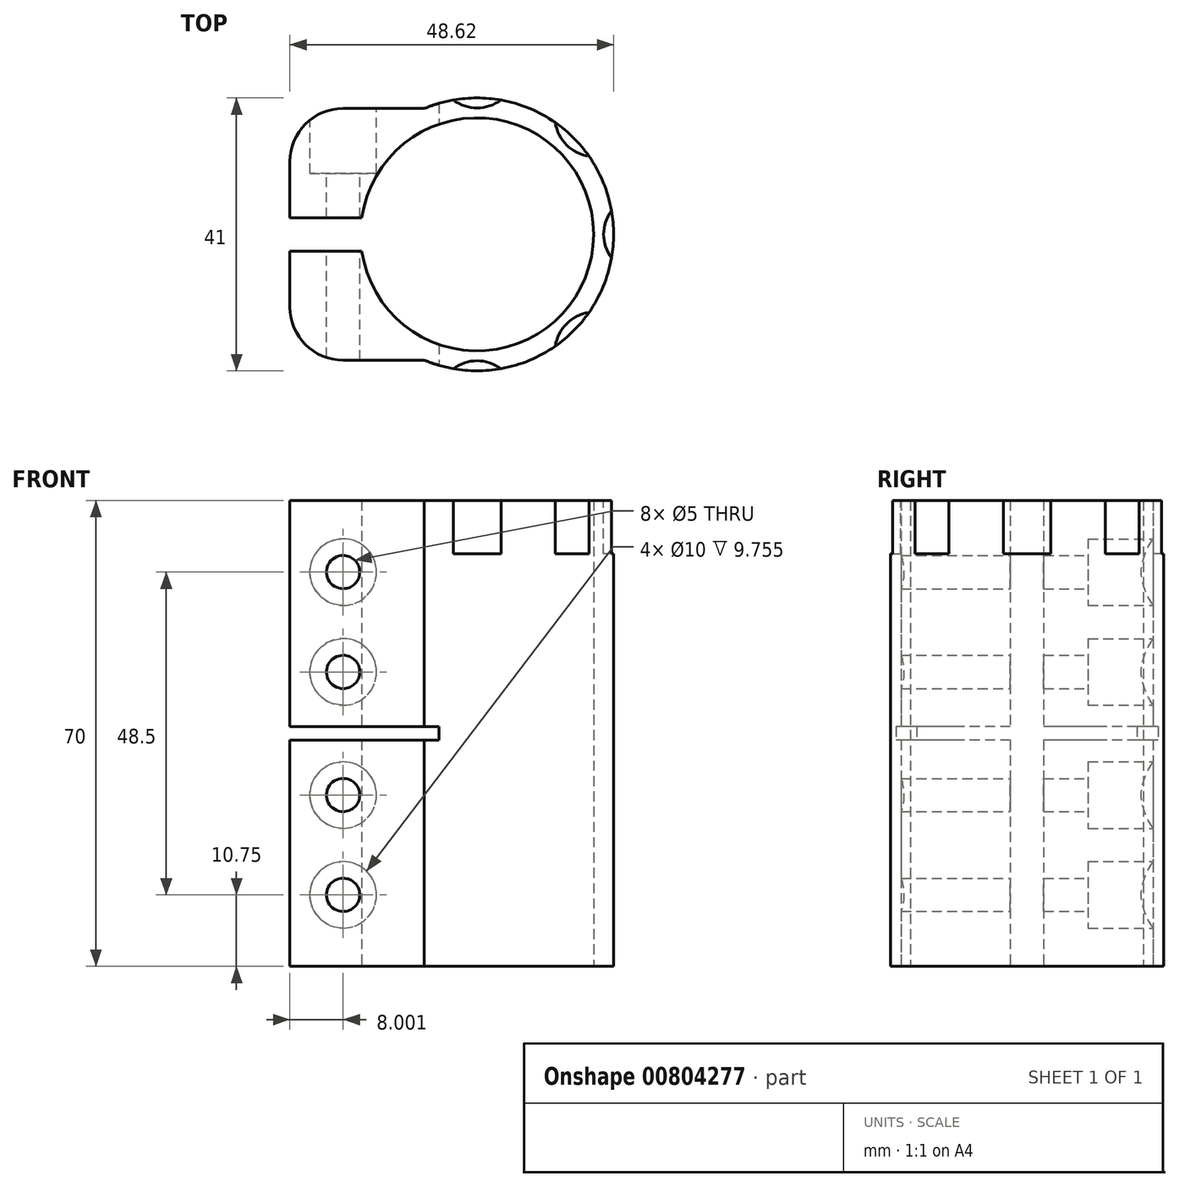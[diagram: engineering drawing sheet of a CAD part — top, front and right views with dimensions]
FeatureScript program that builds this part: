
annotation { "Feature Type Name" : "Feature", "Feature Type Description" : "" }
export const myFeature = defineFeature(function(context is Context, id is Id, definition is map)
    precondition{}
    {
        {
            var Q0;
            Q0=qCreatedBy(makeId("Top.planeOp"),FACE);
            var sketch = newSketch(context, id + "F0", { "sketchPlane" : qUnion([Q0])});
            skArc(sketch, "E0", {"start": v(-17.32, -2.5) * mm, "mid": v(17.5, 0) * mm, "end": v(-17.32, 2.5) * mm});
            skArc(sketch, "E1", {"start": v(-7.92, -18.9) * mm, "mid": v(20.5, 0) * mm, "end": v(-7.92, 18.9) * mm});
            skLineSegment(sketch, "E2", {"start": v(-17.32, 2.5) * mm, "end": v(-28.12, 2.5) * mm});
            skLineSegment(sketch, "E3", {"start": v(-28.12, 2.5) * mm, "end": v(-28.12, 10.9) * mm});
            skLineSegment(sketch, "E4", {"start": v(-20.12, 18.9) * mm, "end": v(-7.92, 18.9) * mm});
            skPoint(sketch, "E5.visualSharp", {"position": v(-28.12, 18.9) * mm});
            skArc(sketch, "E5.filletArc", {"start": v(-20.12, 18.9) * mm, "mid": v(-25.78, 16.57) * mm, "end": v(-28.12, 10.9) * mm});
            skLineSegment(sketch, "E6", {"start": v(0, 0) * mm, "end": v(42.18, 0) * mm, "construction": true});
            skLineSegment(sketch, "E7.MirrorCS", {"start": v(-20.12, -18.9) * mm, "end": v(-7.92, -18.9) * mm});
            skArc(sketch, "E8.MirrorCS", {"start": v(-20.12, -18.9) * mm, "mid": v(-25.78, -16.57) * mm, "end": v(-28.12, -10.9) * mm});
            skLineSegment(sketch, "E9.MirrorCS", {"start": v(-28.12, -2.5) * mm, "end": v(-28.12, -10.9) * mm});
            skLineSegment(sketch, "E10.MirrorCS", {"start": v(-17.32, -2.5) * mm, "end": v(-28.12, -2.5) * mm});
            skSolve(sketch);
        }
        {
            var Q0;
            Q0 = qSketchRegion(id + "F0", true);
            extrude(context, id + "F1", {"entities" : qUnion([Q0]), "endBound" : BoundingType.SYMMETRIC, "depth" : 70 * mm, "offsetDistance" : 25 * mm});
        }
        {
            var Q0;
            Q0=makeQuery(id+"F1.opExtrude","SWEPT_FACE",FACE,{"disambiguationData":[OSD([sQuery(id+"F0.wireOp",EDGE,"E4")])]});
            var sketch = newSketch(context, id + "F2", { "sketchPlane" : qUnion([Q0])});
            skPoint(sketch, "E11", {"position": v(20.12, -24.25) * mm});
            skPoint(sketch, "E12", {"position": v(20.12, -9.25) * mm});
            skPoint(sketch, "E13", {"position": v(20.12, 9.25) * mm});
            skPoint(sketch, "E14", {"position": v(20.12, 24.25) * mm});
            skSolve(sketch);
        }
        {
            var Q0;
            Q0=sQuery(id+"F2.wireOp",VERTEX,"E11");
            var Q1;
            Q1=sQuery(id+"F2.wireOp",VERTEX,"E12");
            var Q2;
            Q2=sQuery(id+"F2.wireOp",VERTEX,"E13");
            var Q3;
            Q3=sQuery(id+"F2.wireOp",VERTEX,"E14");
            var Q4;
            Q4=makeQuery(id+"F1.opExtrude","SWEPT_BODY",BODY,{"disambiguationData":[OSD([sQuery(id+"F0.wireOp",EDGE,"E0"),sQuery(id+"F0.wireOp",EDGE,"E1"),sQuery(id+"F0.wireOp",EDGE,"E2"),sQuery(id+"F0.wireOp",EDGE,"E3"),sQuery(id+"F0.wireOp",EDGE,"E4"),sQuery(id+"F0.wireOp",EDGE,"E5.filletArc"),sQuery(id+"F0.wireOp",EDGE,"E7.MirrorCS"),sQuery(id+"F0.wireOp",EDGE,"E8.MirrorCS"),sQuery(id+"F0.wireOp",EDGE,"E9.MirrorCS"),sQuery(id+"F0.wireOp",EDGE,"E10.MirrorCS")])]});
            hole(context, id + "F3", {"style" : HoleStyle.C_BORE, "endStyle" : HoleEndStyle.THROUGH, "holeDiameter" : 5 * mm, "cBoreDiameter" : 10 * mm, "cBoreDepth" : 8 * mm, "majorDiameter" : 5 * mm, "isTappedThrough" : true, "tappedDepth" : 12 * mm, "tapClearance" : 3, "locations" : qUnion([Q0, Q1, Q2, Q3]), "scope" : qUnion([Q4])});
        }
        {
            var Q0;
            Q0=qCreatedBy(makeId("Front.planeOp"),FACE);
            var sketch = newSketch(context, id + "F4", { "sketchPlane" : qUnion([Q0])});
            skLineSegment(sketch, "E15.bottom", {"start": v(-5.72, 1) * mm, "end": v(-28.12, 1) * mm});
            skLineSegment(sketch, "E15.top", {"start": v(-5.72, -1) * mm, "end": v(-28.12, -1) * mm});
            skLineSegment(sketch, "E15.left", {"start": v(-5.72, 1) * mm, "end": v(-5.72, -1) * mm});
            skLineSegment(sketch, "E15.right", {"start": v(-28.12, 1) * mm, "end": v(-28.12, -1) * mm});
            skSolve(sketch);
        }
        {
            var Q0;
            Q0=makeQuery(id+"F4.imprint","IMPRINT",FACE,{"disambiguationData":[TD([[makeQuery(id+"F4.imprint","IMPRINT",EDGE,{"derivedFrom":sQuery(id+"F4.wireOp",EDGE,"E15.bottom")}),1.0]])]});
            extrude(context, id + "F5", {"entities" : qUnion([Q0]), "operationType" : NewBodyOperationType.REMOVE, "endBound" : BoundingType.SYMMETRIC, "oppositeDirection" : true, "depth" : 50 * mm, "offsetDistance" : 25 * mm, "hasSecondDirection" : true, "secondDirectionOppositeDirection" : false, "secondDirectionDepth" : 25 * mm});
        }
        {
            var Q0;
            Q0=makeQuery(id+"F1.opExtrude","CAP_FACE",FACE,{"disambiguationData":[OSD([sQuery(id+"F0.wireOp",EDGE,"E0"),sQuery(id+"F0.wireOp",EDGE,"E1"),sQuery(id+"F0.wireOp",EDGE,"E2"),sQuery(id+"F0.wireOp",EDGE,"E3"),sQuery(id+"F0.wireOp",EDGE,"E4"),sQuery(id+"F0.wireOp",EDGE,"E5.filletArc"),sQuery(id+"F0.wireOp",EDGE,"E7.MirrorCS"),sQuery(id+"F0.wireOp",EDGE,"E8.MirrorCS"),sQuery(id+"F0.wireOp",EDGE,"E9.MirrorCS"),sQuery(id+"F0.wireOp",EDGE,"E10.MirrorCS")])],"isStart":false});
            var sketch = newSketch(context, id + "F6", { "sketchPlane" : qUnion([Q0])});
            skCircle(sketch, "E16", {"center": v(0, -25) * mm, "radius": 6 * mm});
            skCircle(sketch, "E17.1.0", {"center": v(17.68, -17.68) * mm, "radius": 6 * mm});
            skCircle(sketch, "E17.2.0", {"center": v(25, 0) * mm, "radius": 6 * mm});
            skCircle(sketch, "E17.3.0", {"center": v(17.68, 17.68) * mm, "radius": 6 * mm});
            skCircle(sketch, "E17.4.0", {"center": v(0, 25) * mm, "radius": 6 * mm});
            skPoint(sketch, "E17.center", {"position": v(0, 0) * mm});
            skLineSegment(sketch, "E17.anchor1", {"start": v(0, 0) * mm, "end": v(0, -25) * mm, "construction": true});
            skLineSegment(sketch, "E17.anchor2", {"start": v(0, 0) * mm, "end": v(0, 25) * mm, "construction": true});
            skSolve(sketch);
        }
        {
            var Q0;
            {var subQ0=sQuery(id+"F6.wireOp",EDGE,"E16");var subQ1=makeQuery(id+"F1.opExtrude","CAP_EDGE",EDGE,{"disambiguationData":[OSD([sQuery(id+"F0.wireOp",EDGE,"E1")])],"isStart":false});var subQ2=makeQuery(id+"F6.imprint","INTERSECT",VERTEX,{"disambiguationData":[OD(0.0)],"derivedFrom":[subQ1,subQ0]});Q0=makeQuery(id+"F6.imprint","IMPRINT",FACE,{"disambiguationData":[TD([[makeQuery(id+"F6.imprint","IMPRINT",EDGE,{"disambiguationData":[TD([[subQ2,1.0]])],"derivedFrom":subQ0}),1.0]])]});}
            var Q1;
            {var subQ0=sQuery(id+"F6.wireOp",EDGE,"E17.1.0");var subQ1=makeQuery(id+"F1.opExtrude","CAP_EDGE",EDGE,{"disambiguationData":[OSD([sQuery(id+"F0.wireOp",EDGE,"E1")])],"isStart":false});var subQ2=makeQuery(id+"F6.imprint","INTERSECT",VERTEX,{"disambiguationData":[OD(0.0)],"derivedFrom":[subQ1,subQ0]});Q1=makeQuery(id+"F6.imprint","IMPRINT",FACE,{"disambiguationData":[TD([[makeQuery(id+"F6.imprint","IMPRINT",EDGE,{"disambiguationData":[TD([[subQ2,1.0]])],"derivedFrom":subQ0}),1.0]])]});}
            var Q2;
            {var subQ0=sQuery(id+"F6.wireOp",EDGE,"E17.2.0");var subQ1=makeQuery(id+"F1.opExtrude","CAP_EDGE",EDGE,{"disambiguationData":[OSD([sQuery(id+"F0.wireOp",EDGE,"E1")])],"isStart":false});var subQ2=makeQuery(id+"F6.imprint","INTERSECT",VERTEX,{"disambiguationData":[OD(0.0)],"derivedFrom":[subQ1,subQ0]});Q2=makeQuery(id+"F6.imprint","IMPRINT",FACE,{"disambiguationData":[TD([[makeQuery(id+"F6.imprint","IMPRINT",EDGE,{"disambiguationData":[TD([[subQ2,1.0]])],"derivedFrom":subQ0}),1.0]])]});}
            var Q3;
            {var subQ0=sQuery(id+"F6.wireOp",EDGE,"E17.3.0");var subQ1=makeQuery(id+"F1.opExtrude","CAP_EDGE",EDGE,{"disambiguationData":[OSD([sQuery(id+"F0.wireOp",EDGE,"E1")])],"isStart":false});var subQ2=makeQuery(id+"F6.imprint","INTERSECT",VERTEX,{"disambiguationData":[OD(0.0)],"derivedFrom":[subQ1,subQ0]});Q3=makeQuery(id+"F6.imprint","IMPRINT",FACE,{"disambiguationData":[TD([[makeQuery(id+"F6.imprint","IMPRINT",EDGE,{"disambiguationData":[TD([[subQ2,-1.0]])],"derivedFrom":subQ0}),1.0]])]});}
            var Q4;
            {var subQ0=sQuery(id+"F6.wireOp",EDGE,"E17.4.0");var subQ1=makeQuery(id+"F1.opExtrude","CAP_EDGE",EDGE,{"disambiguationData":[OSD([sQuery(id+"F0.wireOp",EDGE,"E1")])],"isStart":false});var subQ2=makeQuery(id+"F6.imprint","INTERSECT",VERTEX,{"disambiguationData":[OD(0.0)],"derivedFrom":[subQ1,subQ0]});Q4=makeQuery(id+"F6.imprint","IMPRINT",FACE,{"disambiguationData":[TD([[makeQuery(id+"F6.imprint","IMPRINT",EDGE,{"disambiguationData":[TD([[subQ2,-1.0]])],"derivedFrom":subQ0}),1.0]])]});}
            var Q5;
            {var subQ0=sQuery(id+"F6.wireOp",EDGE,"E17.4.0");var subQ1=makeQuery(id+"F1.opExtrude","CAP_EDGE",EDGE,{"disambiguationData":[OSD([sQuery(id+"F0.wireOp",EDGE,"E1")])],"isStart":false});var subQ2=makeQuery(id+"F6.imprint","INTERSECT",VERTEX,{"disambiguationData":[OD(0.0)],"derivedFrom":[subQ1,subQ0]});Q5=makeQuery(id+"F6.imprint","IMPRINT",FACE,{"disambiguationData":[TD([[makeQuery(id+"F6.imprint","IMPRINT",EDGE,{"disambiguationData":[TD([[subQ2,1.0]])],"derivedFrom":subQ0}),1.0]])]});}
            var Q6;
            {var subQ0=sQuery(id+"F6.wireOp",EDGE,"E17.3.0");var subQ1=makeQuery(id+"F1.opExtrude","CAP_EDGE",EDGE,{"disambiguationData":[OSD([sQuery(id+"F0.wireOp",EDGE,"E1")])],"isStart":false});var subQ2=makeQuery(id+"F6.imprint","INTERSECT",VERTEX,{"disambiguationData":[OD(0.0)],"derivedFrom":[subQ1,subQ0]});Q6=makeQuery(id+"F6.imprint","IMPRINT",FACE,{"disambiguationData":[TD([[makeQuery(id+"F6.imprint","IMPRINT",EDGE,{"disambiguationData":[TD([[subQ2,1.0]])],"derivedFrom":subQ0}),1.0]])]});}
            var Q7;
            {var subQ0=sQuery(id+"F6.wireOp",EDGE,"E17.2.0");var subQ1=makeQuery(id+"F1.opExtrude","CAP_EDGE",EDGE,{"disambiguationData":[OSD([sQuery(id+"F0.wireOp",EDGE,"E1")])],"isStart":false});var subQ2=makeQuery(id+"F6.imprint","INTERSECT",VERTEX,{"disambiguationData":[OD(0.0)],"derivedFrom":[subQ1,subQ0]});Q7=makeQuery(id+"F6.imprint","IMPRINT",FACE,{"disambiguationData":[TD([[makeQuery(id+"F6.imprint","IMPRINT",EDGE,{"disambiguationData":[TD([[subQ2,-1.0]])],"derivedFrom":subQ0}),1.0]])]});}
            var Q8;
            {var subQ0=sQuery(id+"F6.wireOp",EDGE,"E17.1.0");var subQ1=makeQuery(id+"F1.opExtrude","CAP_EDGE",EDGE,{"disambiguationData":[OSD([sQuery(id+"F0.wireOp",EDGE,"E1")])],"isStart":false});var subQ2=makeQuery(id+"F6.imprint","INTERSECT",VERTEX,{"disambiguationData":[OD(0.0)],"derivedFrom":[subQ1,subQ0]});Q8=makeQuery(id+"F6.imprint","IMPRINT",FACE,{"disambiguationData":[TD([[makeQuery(id+"F6.imprint","IMPRINT",EDGE,{"disambiguationData":[TD([[subQ2,-1.0]])],"derivedFrom":subQ0}),1.0]])]});}
            var Q9;
            {var subQ0=sQuery(id+"F6.wireOp",EDGE,"E16");var subQ1=makeQuery(id+"F1.opExtrude","CAP_EDGE",EDGE,{"disambiguationData":[OSD([sQuery(id+"F0.wireOp",EDGE,"E1")])],"isStart":false});var subQ2=makeQuery(id+"F6.imprint","INTERSECT",VERTEX,{"disambiguationData":[OD(0.0)],"derivedFrom":[subQ1,subQ0]});Q9=makeQuery(id+"F6.imprint","IMPRINT",FACE,{"disambiguationData":[TD([[makeQuery(id+"F6.imprint","IMPRINT",EDGE,{"disambiguationData":[TD([[subQ2,-1.0]])],"derivedFrom":subQ0}),1.0]])]});}
            extrude(context, id + "F7", {"entities" : qUnion([Q0, Q1, Q2, Q3, Q4, Q5, Q6, Q7, Q8, Q9]), "operationType" : NewBodyOperationType.REMOVE, "oppositeDirection" : true, "depth" : 8 * mm, "offsetDistance" : 25 * mm});
        }
    });
